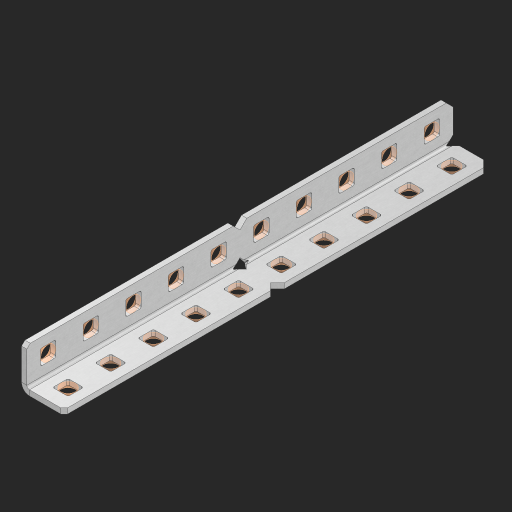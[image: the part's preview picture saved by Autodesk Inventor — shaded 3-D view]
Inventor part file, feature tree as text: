
AUTODESK INVENTOR PART (.ipt)
format: ipt  version: 2023 (Build 270158000, 158)  size: 608,256 bytes
history: native  units: in
note: dims shown in document units (in); Inventor stores cm internally (conversion verified against a paired STEP export)
features: other x26, extrude x21, sheet_metal_op x8, sketch x5, pattern_linear x1, mirror x1, chamfer x1
ambient origin geometry x8: Origin, YZ Plane, XZ Plane, XY Plane, X Axis, Y Axis, Z Axis, Center Point
bodies: Solid1 (feature_tree), Body (feature_tree)
feature tree (63):
  sheet_metal_op  "Flanges"
  sheet_metal_op  "Body Pattern"
  other  "Arc Length"
  pattern_linear  "Notch Pattern"  Spacing1=0.125in  [1 undecoded]
  other  "Diagonal Plane"
  mirror  "Everything Mirrored"
  chamfer  "End Chamfer"
  sketch  "Sketch1"  dims[d0=0.5in]
  other  "Plate1"
  sketch  "Sketch2"  dims[d1=5.0in]
  other  "Plate2"
  sheet_metal_op  "Bend1"
  sheet_metal_op  "Corner1"
  sketch  "Sketch8"  dims[d2=0.0625in]
  sketch  "Sketch9"  dims[d3=0.0625in]
  other  "Srf91"
  sheet_metal_op  "Body Pattern Sketch"
  other  "Srf92"
  sketch  "Sketch13"  dims[d4=0.0312in d5=0.125in d6=0.0625in d7=0.5in d8=90.0deg d9=0.0312in d10=0.25in d11=0.0625in d12=0.0625in d49=0.182in d50=0.02in d52=0.25in d53=0.0625in d54=0.0in d55=0.172in d56=1.0in d57=0.0in d85=0.1473in d86=0.1782in d89=0.0625in d90=0.0in d91=0.04in d92=0.0491in d95=2.5in d96=0.04in d97=0.25in d98=45.0deg d123=0.204in d126=0.0491in d127=0.1473in d128=0.08in d129=0.04in d130=2.5in d131=3.937in d133=0.5in d134=0.3937in d136=1.0in]
  other  "Srf856"
  other  "Srf857"
  other  "Srf858"
  other  "Srf859"
  other  "Srf860"
  other  "Srf861"
  other  "Srf1275"
  other  "Srf1276"
  other  "Srf1278"
  other  "Srf1279"
  other  "Srf1280"
  other  "Srf1281"
  other  "Srf1282"
  other  "Srf1283"
  other  "Srf1383"
  other  "Srf1384"
  other  "Srf1385"
  other  "Srf1475"
  other  "Srf1476"
  other  "Srf1477"
  sheet_metal_op  "Body Stamp"
  sheet_metal_op  "Body Circle"
  sheet_metal_op  "Notch"
  extrude  "ExtrusionSrf92"  Depth=0.0625in
  extrude  "ExtrusionSrf856"  Depth=0.5in TaperAngle=90.0deg
  extrude  "ExtrusionSrf857"  Depth=0.25in
  extrude  "ExtrusionSrf858"  Depth=0.0625in
  extrude  "ExtrusionSrf859"  Depth=0.0625in
  extrude  "ExtrusionSrf860"  Depth=0.3937in
  extrude  "ExtrusionSrf861"  Depth=0.02in
  extrude  "ExtrusionSrf1275"  Depth=0.25in
  extrude  "ExtrusionSrf1276"  Depth=0.0625in
  extrude  "ExtrusionSrf1277"  TaperAngle=0.0deg  [1 undecoded]
  extrude  "ExtrusionSrf1278"  Depth=0.3937in
  extrude  "ExtrusionSrf1279"  Depth=0.3937in TaperAngle=0.0deg
  extrude  "ExtrusionSrf1280"  Depth=0.3937in
  extrude  "ExtrusionSrf1281"  Depth=0.3937in
  extrude  "ExtrusionSrf1282"  Depth=0.0625in
  extrude  "ExtrusionSrf1383"  Depth=0.3937in TaperAngle=0.0deg
  extrude  "ExtrusionSrf1384"  Depth=2.5in
  extrude  "ExtrusionSrf1385"  Depth=0.25in TaperAngle=45.0deg
  extrude  "ExtrusionSrf1475"  Depth=0.3937in
  extrude  "ExtrusionSrf1476"  Depth=0.3937in
  extrude  "ExtrusionSrf1477"  Depth=0.3937in
note: 2 required parameter values undecoded (feature->parameter linkage not recoverable at this tier; creation-order binding heuristic only, values carry confidence <= 0.55)
